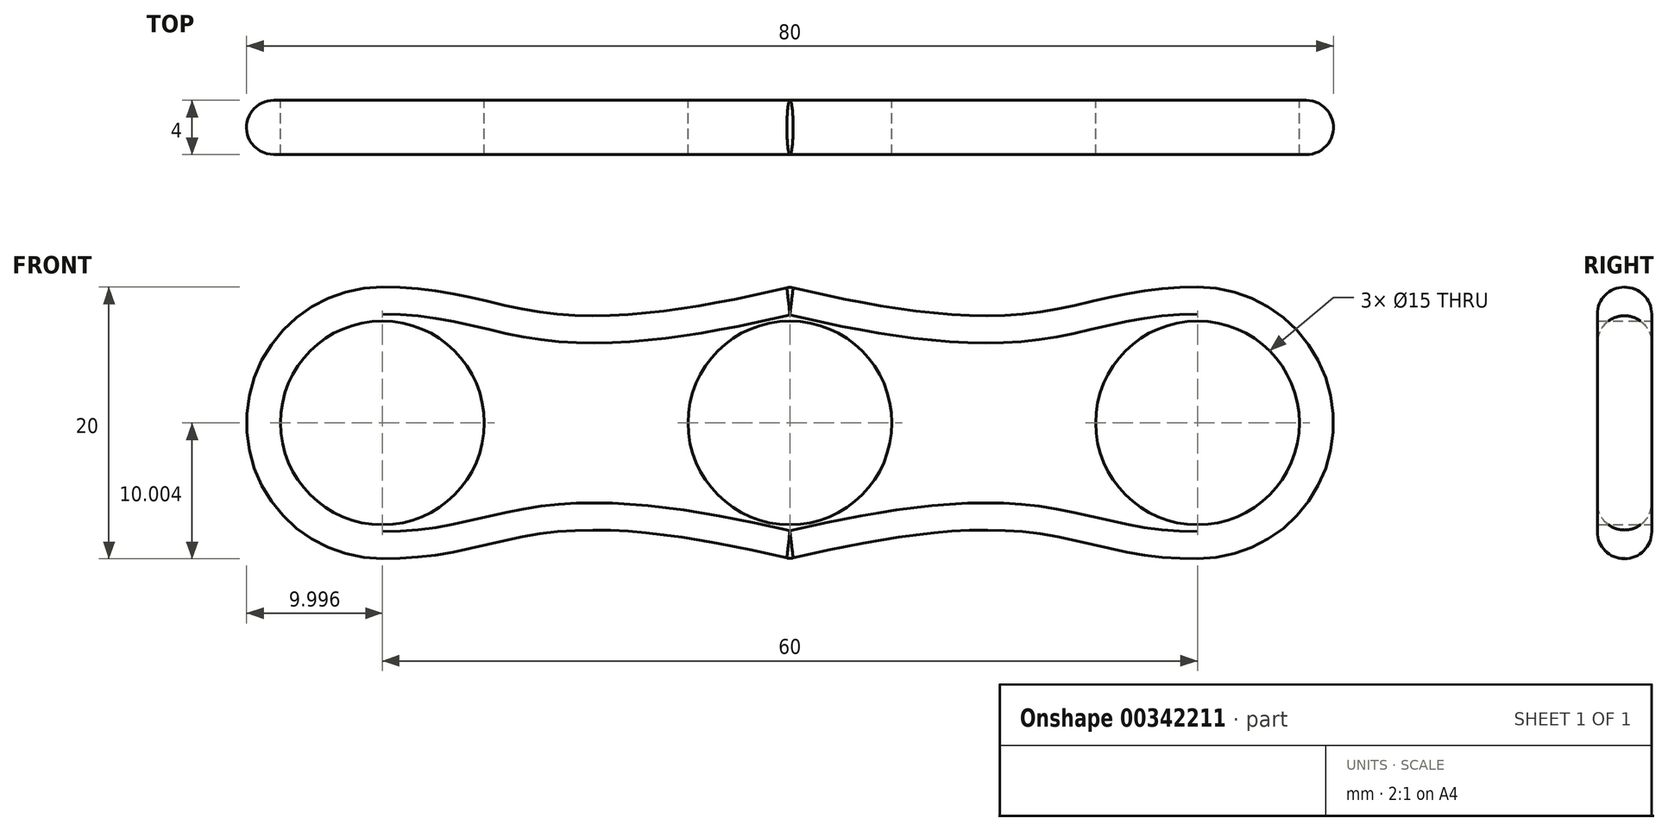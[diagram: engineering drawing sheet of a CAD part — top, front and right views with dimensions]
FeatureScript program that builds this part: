
annotation { "Feature Type Name" : "Feature", "Feature Type Description" : "" }
export const myFeature = defineFeature(function(context is Context, id is Id, definition is map)
    precondition{}
    {
        {
            var Q0;
            Q0=qCreatedBy(makeId("Front.planeOp"),FACE);
            var sketch = newSketch(context, id + "F0", { "sketchPlane" : qUnion([Q0])});
            skLineSegment(sketch, "E0.left", {"start": v(-32.53, 13.05) * mm, "end": v(-32.53, 13.05) * mm});
            skLineSegment(sketch, "E0.right", {"start": v(47.47, 13.05) * mm, "end": v(47.47, 13.05) * mm});
            skLineSegment(sketch, "E1", {"start": v(7.47, 23.05) * mm, "end": v(7.47, 3.05) * mm, "construction": true});
            skCircle(sketch, "E2", {"center": v(7.47, 13.05) * mm, "radius": 7.5 * mm});
            skLineSegment(sketch, "E3", {"start": v(27.47, 23.05) * mm, "end": v(27.47, 3.05) * mm, "construction": true});
            skLineSegment(sketch, "E4.MirrorCS", {"start": v(-12.53, 23.05) * mm, "end": v(-12.53, 3.05) * mm, "construction": true});
            skLineSegment(sketch, "E5", {"start": v(-32.53, 13.05) * mm, "end": v(47.47, 13.05) * mm, "construction": true});
            skCircle(sketch, "E6", {"center": v(37.47, 13.05) * mm, "radius": 7.5 * mm});
            skCircle(sketch, "E7.MirrorC", {"center": v(-22.53, 13.05) * mm, "radius": 7.5 * mm});
            skPoint(sketch, "E8.visualSharp", {"position": v(-32.53, 23.05) * mm});
            skArc(sketch, "E8.filletArc", {"start": v(-22.53, 23.05) * mm, "mid": v(-29.6, 20.13) * mm, "end": v(-32.53, 13.05) * mm});
            skPoint(sketch, "E9.visualSharp", {"position": v(-32.53, 3.05) * mm});
            skArc(sketch, "E9.filletArc", {"start": v(-32.53, 13.05) * mm, "mid": v(-29.6, 5.98) * mm, "end": v(-22.53, 3.05) * mm});
            skPoint(sketch, "E10.visualSharp", {"position": v(47.47, 23.05) * mm});
            skArc(sketch, "E10.filletArc", {"start": v(47.47, 13.05) * mm, "mid": v(44.54, 20.13) * mm, "end": v(37.47, 23.05) * mm});
            skPoint(sketch, "E11.visualSharp", {"position": v(47.47, 3.05) * mm});
            skArc(sketch, "E11.filletArc", {"start": v(37.47, 3.05) * mm, "mid": v(44.54, 5.98) * mm, "end": v(47.47, 13.05) * mm});
            skFitSpline(sketch, "E12", {"points": [v(-22.53, 23.05) * mm, v(7.47, 23.05) * mm], "startDerivative": vector(30, 0) * mm, "endDerivative": vector(60, 14.29) * mm});
            skFitSpline(sketch, "E13.MirrorCS", {"points": [v(37.47, 23.05) * mm, v(7.47, 23.05) * mm], "startDerivative": vector(-30, 0) * mm, "endDerivative": vector(-60, 14.29) * mm});
            skFitSpline(sketch, "E14.MirrorCS", {"points": [v(-22.53, 3.05) * mm, v(7.47, 3.05) * mm], "startDerivative": vector(30, 0) * mm, "endDerivative": vector(60, -14.29) * mm});
            skFitSpline(sketch, "E15.MirrorCS", {"points": [v(37.47, 3.05) * mm, v(7.47, 3.05) * mm], "startDerivative": vector(-30, 0) * mm, "endDerivative": vector(-60, -14.29) * mm});
            skSolve(sketch);
        }
        {
            var Q0;
            Q0=makeQuery(id+"F0.imprint","IMPRINT",FACE,{"disambiguationData":[TD([[makeQuery(id+"F0.imprint","IMPRINT",EDGE,{"derivedFrom":sQuery(id+"F0.wireOp",EDGE,"E2")}),-1.0]])]});
            extrude(context, id + "F1", {"entities" : qUnion([Q0]), "depth" : 4 * mm});
        }
        {
            var Q0;
            Q0=makeQuery(id+"F1.opExtrude","CAP_EDGE",EDGE,{"disambiguationData":[OSD([sQuery(id+"F0.wireOp",EDGE,"E12")])],"isStart":false});
            var Q1;
            Q1=makeQuery(id+"F1.opExtrude","CAP_EDGE",EDGE,{"disambiguationData":[OSD([sQuery(id+"F0.wireOp",EDGE,"E13.MirrorCS")])],"isStart":false});
            var Q2;
            Q2=makeQuery(id+"F1.opExtrude","CAP_EDGE",EDGE,{"disambiguationData":[OSD([sQuery(id+"F0.wireOp",EDGE,"E15.MirrorCS")])],"isStart":true});
            var Q3;
            Q3=makeQuery(id+"F1.opExtrude","CAP_EDGE",EDGE,{"disambiguationData":[OSD([sQuery(id+"F0.wireOp",EDGE,"E14.MirrorCS")])],"isStart":true});
            fillet(context, id + "F2", {"entities" : qUnion([Q0, Q1, Q2, Q3]), "radius" : 2 * mm, "tangentPropagation" : true, "allowEdgeOverflow" : false});
        }
        {
            var Q0;
            Q0=makeQuery(id+"F2.opFillet","BLEND_EDGE",EDGE,{"blendedFrom":[makeQuery(id+"F1.opExtrude","CAP_EDGE",EDGE,{"disambiguationData":[OSD([sQuery(id+"F0.wireOp",EDGE,"E12")])],"isStart":false}),makeQuery(id+"F1.opExtrude","CAP_EDGE",EDGE,{"disambiguationData":[OSD([sQuery(id+"F0.wireOp",EDGE,"E13.MirrorCS")])],"isStart":false})],"blendedInto":[]});
            var Q1;
            Q1=makeQuery(id+"F2.opFillet","BLEND_EDGE",EDGE,{"blendedFrom":[makeQuery(id+"F1.opExtrude","CAP_EDGE",EDGE,{"disambiguationData":[OSD([sQuery(id+"F0.wireOp",EDGE,"E12")])],"isStart":true}),makeQuery(id+"F1.opExtrude","CAP_EDGE",EDGE,{"disambiguationData":[OSD([sQuery(id+"F0.wireOp",EDGE,"E13.MirrorCS")])],"isStart":true})],"blendedInto":[]});
            var Q2;
            Q2=makeQuery(id+"F2.opFillet","BLEND_EDGE",EDGE,{"blendedFrom":[makeQuery(id+"F1.opExtrude","CAP_EDGE",EDGE,{"disambiguationData":[OSD([sQuery(id+"F0.wireOp",EDGE,"E14.MirrorCS")])],"isStart":false}),makeQuery(id+"F1.opExtrude","CAP_EDGE",EDGE,{"disambiguationData":[OSD([sQuery(id+"F0.wireOp",EDGE,"E15.MirrorCS")])],"isStart":false})],"blendedInto":[]});
            fillet(context, id + "F3", {"entities" : qUnion([Q0, Q1, Q2]), "radius" : 1 * mm, "tangentPropagation" : true, "allowEdgeOverflow" : false});
        }
    });
